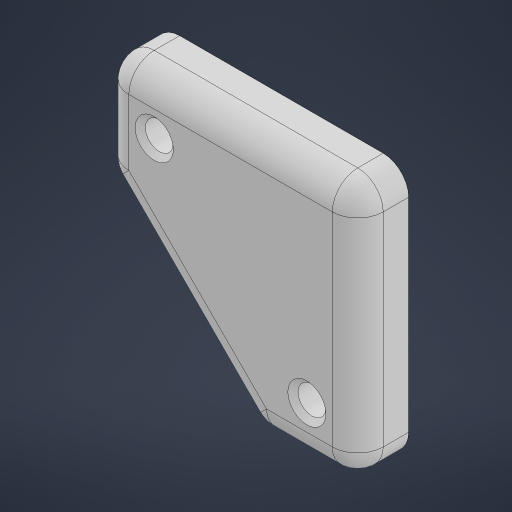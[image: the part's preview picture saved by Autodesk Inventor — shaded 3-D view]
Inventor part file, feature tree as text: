
AUTODESK INVENTOR PART (.ipt)
format: ipt  version: 2024 (Build 280153000, 153)  size: 220,672 bytes
history: native  units: mm
features: extrude x2, fillet x2, sketch x2, other x1, chamfer x1
ambient origin geometry x8: Origin, YZ Plane, XZ Plane, XY Plane, X Axis, Y Axis, Z Axis, Center Point
bodies: Body1 (feature_tree)
feature tree (8):
  other  "솔리드1"
  extrude  "돌출1"  Depth=50.0mm
  fillet  "모깎기1"  Radius=50.0mm
  fillet  "모깎기2"  Radius=20.0mm
  extrude  "돌출2"  Depth=20.0mm
  chamfer  "모따기1"  Distance=10.0mm
  sketch  "스케치1"
  sketch  "스케치2"
